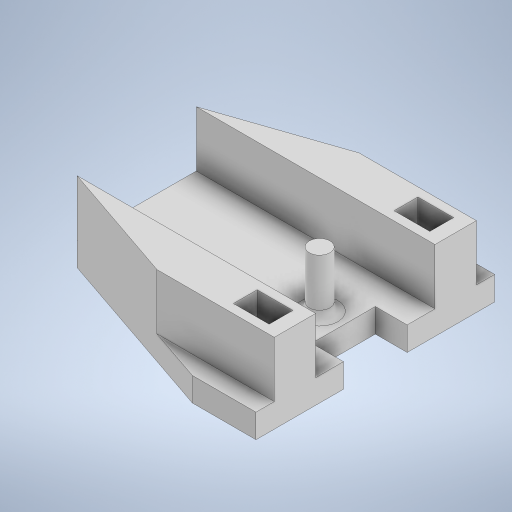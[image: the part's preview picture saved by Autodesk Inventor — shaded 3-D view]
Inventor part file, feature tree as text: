
AUTODESK INVENTOR PART (.ipt)
format: ipt  version: 2024.2 (Build 282272000, 272)  size: 320,512 bytes
history: native  units: mm
features: extrude x4, sketch x4, fillet x1
ambient origin geometry x8: Origin, YZ Plane, XZ Plane, XY Plane, X Axis, Y Axis, Z Axis, Center Point
bodies: Solid1 (feature_tree)
feature tree (9):
  extrude  "Extrusion1"  Depth=8.0mm
  extrude  "Extrusion2"  Depth=3.0mm
  extrude  "Extrusion3"  Depth=17.2mm
  extrude  "Extrusion4"  Depth=1.75mm
  fillet  "Fillet1"  Radius=15.0mm
  sketch  "Sketch1"  dims[d0=30.0mm d1=8.0mm]
  sketch  "Sketch2"  dims[d2=4.5mm d3=3.0mm]
  sketch  "Sketch3"  dims[d4=3.0mm d5=17.2mm]
  sketch  "Sketch4"  dims[d6=3.4mm d7=1.75mm d8=15.0mm d10=7.5mm d11=22.0mm d12=22.0mm d13=3.0mm d14=0.0mm d17=2.6mm d21=1.1mm d22=1.1mm d23=15.0mm d24=7.0mm d25=7.0mm d26=0.0mm d27=0.0mm d28=0.0mm d29=3.0mm d30=8.0mm d31=3.5mm d32=0.0mm d33=0.0mm d34=1.0mm]
